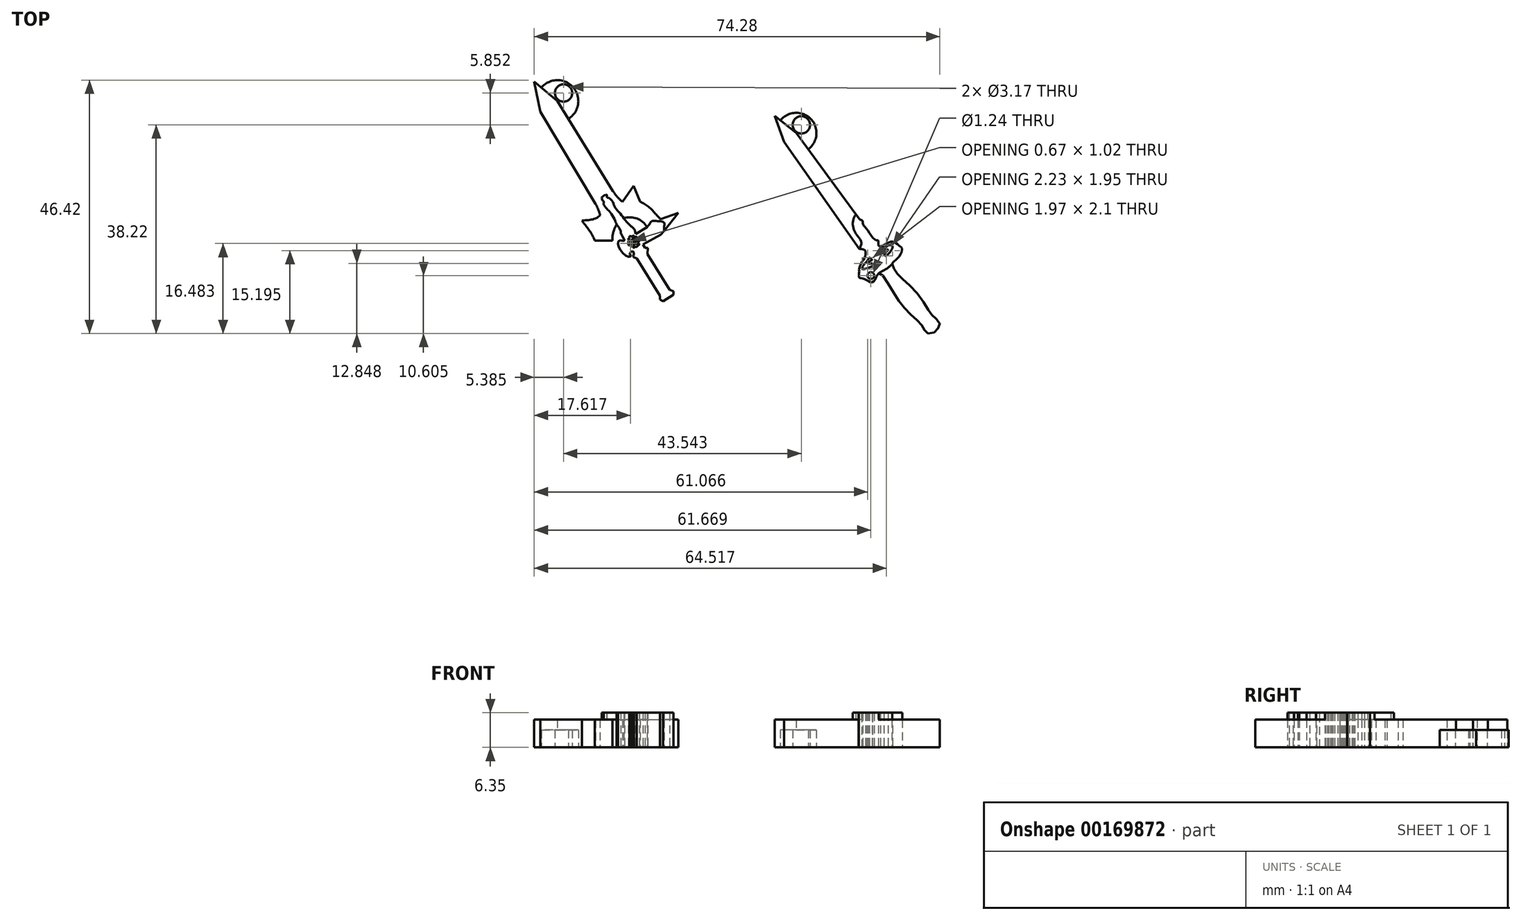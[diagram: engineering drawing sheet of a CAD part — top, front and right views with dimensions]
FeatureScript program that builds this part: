
annotation { "Feature Type Name" : "Feature", "Feature Type Description" : "" }
export const myFeature = defineFeature(function(context is Context, id is Id, definition is map)
    precondition{}
    {
        {
            var Q0;
            Q0=qCreatedBy(makeId("Top.planeOp"),FACE);
            var sketch = newSketch(context, id + "F0", { "sketchPlane" : qUnion([Q0])});
            skLineSegment(sketch, "E0", {"start": v(-47.89, 9.47) * mm, "end": v(-46.77, 3.95) * mm});
            skLineSegment(sketch, "E1", {"start": v(-47.89, 9.47) * mm, "end": v(-43.64, 5.88) * mm});
            skLineSegment(sketch, "E2", {"start": v(-46.77, 3.95) * mm, "end": v(-36.67, -12.95) * mm});
            skLineSegment(sketch, "E3", {"start": v(-43.64, 5.88) * mm, "end": v(-33.47, -10.58) * mm});
            skFitSpline(sketch, "E4", {"points": [v(-36.67, -12.95) * mm, v(-36.26, -13.75) * mm, v(-35.92, -14.65) * mm, v(-35.87, -15.06) * mm, v(-36.67, -15.62) * mm, v(-37.77, -15.9) * mm, v(-39.13, -15.98) * mm], "startDerivative": vector(2.9, -5.08) * mm, "endDerivative": vector(-7.18, 0.14) * mm});
            skFitSpline(sketch, "E5", {"points": [v(-39.13, -15.98) * mm, v(-38.65, -16.7) * mm, v(-37.46, -18.3) * mm, v(-36.8, -19.7) * mm], "startDerivative": vector(1.55, -2.5) * mm, "endDerivative": vector(1.54, -3.95) * mm});
            skLineSegment(sketch, "E6", {"start": v(-36.8, -19.7) * mm, "end": v(-33.56, -19.7) * mm});
            skFitSpline(sketch, "E7", {"points": [v(-33.56, -19.7) * mm, v(-33.56, -19.03) * mm, v(-33.26, -17.7) * mm, v(-32.82, -16.73) * mm], "startDerivative": vector(-0.15, 2.21) * mm, "endDerivative": vector(1.34, 2.63) * mm});
            skFitSpline(sketch, "E8", {"points": [v(-32.82, -16.73) * mm, v(-32, -18) * mm, v(-32.05, -18.37) * mm, v(-31.33, -19.7) * mm, v(-31.77, -19.7) * mm, v(-32.36, -19.7) * mm, v(-32.51, -20.21) * mm, v(-32.2, -21.22) * mm, v(-31.3, -22.27) * mm, v(-30.43, -22.65) * mm, v(-30.2, -22.5) * mm, v(-30.4, -22.17) * mm, v(-30.15, -21.78) * mm, v(-29.87, -21.6) * mm, v(-29.64, -21.88) * mm, v(-29.69, -22.4) * mm, v(-29.8, -22.63) * mm, v(-29.1, -22.93) * mm], "startDerivative": vector(13.43, -16.85) * mm, "endDerivative": vector(15.22, -4.58) * mm});
            skLineSegment(sketch, "E9", {"start": v(-29.1, -22.93) * mm, "end": v(-24.87, -29.77) * mm});
            skLineSegment(sketch, "E10", {"start": v(-23.1, -28.68) * mm, "end": v(-27.13, -22.17) * mm});
            skLineSegment(sketch, "E11", {"start": v(-24.87, -29.77) * mm, "end": v(-24.87, -30.5) * mm});
            skLineSegment(sketch, "E12", {"start": v(-24.87, -30.5) * mm, "end": v(-24.3, -30.8) * mm});
            skLineSegment(sketch, "E13", {"start": v(-24.3, -30.8) * mm, "end": v(-22.35, -29.6) * mm});
            skLineSegment(sketch, "E14", {"start": v(-22.35, -29.6) * mm, "end": v(-22.35, -28.93) * mm});
            skLineSegment(sketch, "E15", {"start": v(-22.35, -28.93) * mm, "end": v(-23.1, -28.68) * mm});
            skFitSpline(sketch, "E16", {"points": [v(-33.47, -10.58) * mm, v(-32.53, -11.84) * mm, v(-31.7, -12.56) * mm], "startDerivative": vector(1.7, -2.5) * mm, "endDerivative": vector(1.85, -1.41) * mm});
            skLineSegment(sketch, "E17", {"start": v(-31.7, -12.56) * mm, "end": v(-29.65, -9.67) * mm});
            skLineSegment(sketch, "E18", {"start": v(-29.65, -9.67) * mm, "end": v(-28.47, -12.56) * mm});
            skFitSpline(sketch, "E19", {"points": [v(-28.47, -12.56) * mm, v(-26.96, -13.47) * mm, v(-25.44, -15.02) * mm, v(-24.72, -15.78) * mm], "startDerivative": vector(4.38, -2.16) * mm, "endDerivative": vector(2.44, -2.49) * mm});
            skLineSegment(sketch, "E20", {"start": v(-24.72, -15.78) * mm, "end": v(-21.5, -14.6) * mm});
            skLineSegment(sketch, "E21", {"start": v(-21.5, -14.6) * mm, "end": v(-24.08, -17.94) * mm});
            skLineSegment(sketch, "E22", {"start": v(-24.08, -17.94) * mm, "end": v(-24.72, -18.63) * mm});
            skLineSegment(sketch, "E23", {"start": v(-24.72, -18.63) * mm, "end": v(-27.94, -20.4) * mm});
            skLineSegment(sketch, "E24", {"start": v(-27.94, -20.4) * mm, "end": v(-27.61, -21) * mm});
            skLineSegment(sketch, "E25", {"start": v(-27.61, -21) * mm, "end": v(-27.09, -21) * mm});
            skLineSegment(sketch, "E26", {"start": v(-27.09, -21) * mm, "end": v(-27.13, -22.17) * mm});
            skArc(sketch, "E27", {"start": v(-27.22, -17.2) * mm, "mid": v(-29.07, -15.64) * mm, "end": v(-31.48, -15.61) * mm});
            skFitSpline(sketch, "E28", {"points": [v(-31.48, -15.61) * mm, v(-30.14, -17.07) * mm, v(-29.6, -17.52) * mm, v(-29.37, -18.14) * mm, v(-29.28, -18.48) * mm], "startDerivative": vector(3.75, -4.48) * mm, "endDerivative": vector(0.5, -1.86) * mm});
            skFitSpline(sketch, "E29", {"points": [v(-29.28, -18.48) * mm, v(-27.22, -17.2) * mm], "startDerivative": vector(2.06, 1.28) * mm, "endDerivative": vector(2.06, 1.28) * mm});
            skFitSpline(sketch, "E30", {"points": [v(-35.52, -11.9) * mm, v(-35.18, -11.48) * mm, v(-34.54, -11.32) * mm, v(-34.58, -11.68) * mm, v(-34.14, -11.93) * mm, v(-33.38, -12.83) * mm, v(-33.14, -13.59) * mm, v(-32.29, -14.55) * mm, v(-31.48, -15.61) * mm], "startDerivative": vector(1.05, 4.71) * mm, "endDerivative": vector(4.53, -6.67) * mm});
            skFitSpline(sketch, "E31", {"points": [v(-35.52, -11.9) * mm, v(-35.38, -12.3) * mm, v(-35.16, -12.49) * mm, v(-35.16, -13) * mm, v(-34.56, -13.9) * mm, v(-34.03, -14.4) * mm, v(-33.12, -15.9) * mm, v(-32.82, -16.73) * mm], "startDerivative": vector(0.68, -4.36) * mm, "endDerivative": vector(1.38, -4.7) * mm});
            skFitSpline(sketch, "E32", {"points": [v(-27.22, -17.2) * mm, v(-26.75, -16.63) * mm, v(-26.37, -16.13) * mm, v(-25.7, -16.1) * mm, v(-24.54, -16.17) * mm, v(-24.08, -16.48) * mm, v(-24.1, -17.4) * mm, v(-24.08, -17.94) * mm], "startDerivative": vector(3.54, 3.78) * mm, "endDerivative": vector(0.59, -3.93) * mm});
            skFitSpline(sketch, "E33", {"points": [v(-30.42, -18.89) * mm, v(-30.42, -19.17) * mm, v(-30.65, -19.36) * mm, v(-30.56, -19.55) * mm, v(-30.32, -19.47) * mm, v(-29.97, -19.65) * mm, v(-29.84, -19.58) * mm, v(-29.8, -19.14) * mm, v(-29.61, -19) * mm, v(-29.64, -18.8) * mm, v(-29.87, -18.86) * mm, v(-30.03, -18.9) * mm, v(-30.42, -18.89) * mm]});
            skFitSpline(sketch, "E34", {"points": [v(-30.57, -19.7) * mm, v(-30.32, -19.86) * mm, v(-30.02, -19.9) * mm, v(-29.97, -20.22) * mm, v(-29.92, -20.61) * mm, v(-30.05, -20.74) * mm, v(-30.32, -20.46) * mm, v(-30.58, -20.5) * mm, v(-30.6, -20.23) * mm, v(-30.57, -19.7) * mm]});
            skFitSpline(sketch, "E35", {"points": [v(-29.39, -19.06) * mm, v(-29.33, -19.31) * mm, v(-29.47, -19.55) * mm, v(-29.46, -19.8) * mm, v(-29.13, -19.77) * mm, v(-28.84, -19.92) * mm, v(-28.7, -19.83) * mm, v(-28.72, -19.46) * mm, v(-28.96, -19.2) * mm, v(-29.3, -19) * mm, v(-29.39, -19.06) * mm]});
            skFitSpline(sketch, "E36", {"points": [v(-29.61, -20.15) * mm, v(-29.57, -20.54) * mm, v(-29.78, -20.84) * mm, v(-29.7, -20.95) * mm, v(-29.6, -20.93) * mm, v(-29.25, -20.83) * mm, v(-29, -20.78) * mm, v(-28.93, -20.58) * mm, v(-28.65, -20.41) * mm, v(-28.68, -20.3) * mm, v(-29.18, -20.3) * mm, v(-29.4, -20.04) * mm, v(-29.61, -20.15) * mm]});
            skLineSegment(sketch, "E37.bottom", {"start": v(-29.85, -19.7) * mm, "end": v(-29.63, -19.7) * mm});
            skLineSegment(sketch, "E37.top", {"start": v(-29.85, -19.97) * mm, "end": v(-29.63, -19.97) * mm});
            skLineSegment(sketch, "E37.left", {"start": v(-29.85, -19.7) * mm, "end": v(-29.85, -19.97) * mm});
            skLineSegment(sketch, "E37.right", {"start": v(-29.63, -19.7) * mm, "end": v(-29.63, -19.97) * mm});
            skLineSegment(sketch, "E38", {"start": v(-2.15, -1.62) * mm, "end": v(11.63, -21.22) * mm});
            skLineSegment(sketch, "E39", {"start": v(0.1, 0.03) * mm, "end": v(11.63, -15.68) * mm});
            skFitSpline(sketch, "E40", {"points": [v(11.63, -21.22) * mm, v(12.7, -21.48) * mm, v(12.73, -22.53) * mm, v(12.21, -23.47) * mm, v(11.63, -24.82) * mm, v(11.63, -25.48) * mm, v(11.63, -26.45) * mm, v(12.64, -26.72) * mm, v(13.69, -27.29) * mm, v(14.47, -26.93) * mm, v(15.22, -25.63) * mm, v(16.13, -26.33) * mm, v(18.33, -29.88) * mm, v(20.37, -32.5) * mm, v(22.57, -34.57) * mm, v(23.44, -35.75) * mm, v(23.98, -36.6) * mm, v(25.46, -36.47) * mm, v(26.21, -35.57) * mm, v(26.33, -34.66) * mm, v(25.16, -33.55) * mm, v(24.23, -32.29) * mm, v(21.85, -28.89) * mm, v(19.14, -26.33) * mm, v(18.14, -25) * mm, v(17.66, -23.95) * mm, v(18.63, -22.98) * mm, v(19.5, -21.22) * mm, v(19.02, -20.67) * mm, v(18, -19.94) * mm, v(16.82, -20.13) * mm, v(15.38, -20.73) * mm, v(15.13, -20.3) * mm, v(15.1, -19.67) * mm, v(14.6, -19.55) * mm, v(12.97, -17.5) * mm, v(12.3, -16.63) * mm, v(12.24, -16.1) * mm, v(11.88, -15.88) * mm, v(11.63, -15.68) * mm], "startDerivative": vector(56.2, -1.17) * mm, "endDerivative": vector(-16.89, 17.47) * mm});
            skLineSegment(sketch, "E41", {"start": v(-3.86, 3.14) * mm, "end": v(-2.15, -1.62) * mm});
            skLineSegment(sketch, "E42", {"start": v(0.1, 0.03) * mm, "end": v(-3.86, 3.14) * mm});
            skPoint(sketch, "E43.start.orphan", {"position": v(-8.49, 9.47) * mm});
            skFitSpline(sketch, "E44", {"points": [v(14, -23.23) * mm, v(13.35, -23.8) * mm, v(13.68, -23.93) * mm, v(14.8, -23.36) * mm, v(16.7, -21.67) * mm, v(16.9, -21.33) * mm, v(16.2, -21.49) * mm, v(15.98, -21.57) * mm, v(15.38, -20.73) * mm], "startDerivative": vector(-7.7, -5.02) * mm, "endDerivative": vector(-5.02, 8.35) * mm});
            skFitSpline(sketch, "E45", {"points": [v(14, -23.23) * mm, v(13.52, -22.8) * mm, v(12.93, -22.67) * mm, v(12.73, -22.53) * mm], "startDerivative": vector(-1.1, 1.33) * mm, "endDerivative": vector(-0.68, 0.64) * mm});
            skFitSpline(sketch, "E46", {"points": [v(15.22, -25.63) * mm, v(17.13, -24.5) * mm, v(17.66, -23.95) * mm], "startDerivative": vector(3.52, 1.9) * mm, "endDerivative": vector(1.15, 1.43) * mm});
            skCircle(sketch, "E47", {"center": v(13.78, -26.1) * mm, "radius": 0.62 * mm});
            skArc(sketch, "E48", {"start": v(-41.62, 2.62) * mm, "mid": v(-40.74, 8.39) * mm, "end": v(-46.57, 8.36) * mm});
            skCircle(sketch, "E49", {"center": v(-42.5, 7.37) * mm, "radius": 1.59 * mm});
            skArc(sketch, "E50", {"start": v(2.3, -2.95) * mm, "mid": v(2.77, 2.6) * mm, "end": v(-2.8, 2.32) * mm});
            skCircle(sketch, "E51", {"center": v(1.04, 1.52) * mm, "radius": 1.59 * mm});
            skFitSpline(sketch, "E52", {"points": [v(11.03, -14.86) * mm, v(10.62, -15.63) * mm, v(10.48, -16.83) * mm, v(10.75, -17.92) * mm, v(11.47, -19) * mm, v(12.03, -20.1) * mm, v(11.63, -21.22) * mm], "startDerivative": vector(-3.14, -4.88) * mm, "endDerivative": vector(-3.7, -6.63) * mm});
            skFitSpline(sketch, "E53", {"points": [v(15.51, -20.96) * mm, v(17.07, -20.52) * mm, v(17.68, -20.6) * mm, v(17.58, -21.33) * mm, v(16.48, -22.48) * mm, v(16.2, -22.18) * mm], "startDerivative": vector(6.32, 2.09) * mm, "endDerivative": vector(-1.57, 3.48) * mm});
            skFitSpline(sketch, "E54", {"points": [v(13, -23.53) * mm, v(12.3, -24.41) * mm, v(12.22, -24.9) * mm, v(12.92, -24.78) * mm, v(14.13, -24.31) * mm, v(14.04, -23.84) * mm], "startDerivative": vector(-3.42, -3.59) * mm, "endDerivative": vector(-1.61, 3.27) * mm});
            skFitSpline(sketch, "E55", {"points": [v(13, -23.53) * mm, v(13.52, -22.8) * mm], "startDerivative": vector(0.52, 0.73) * mm, "endDerivative": vector(0.52, 0.73) * mm});
            skSolve(sketch);
        }
        {
            var Q0;
            Q0=makeQuery(id+"F0.imprint","IMPRINT",FACE,{"disambiguationData":[TD([[makeQuery(id+"F0.imprint","IMPRINT",EDGE,{"derivedFrom":sQuery(id+"F0.wireOp",EDGE,"E8")}),1.0]])]});
            var Q1;
            {var subQ0=sQuery(id+"F0.wireOp",EDGE,"E44");Q1=makeQuery(id+"F0.imprint","IMPRINT",FACE,{"disambiguationData":[TD([[makeQuery(id+"F0.imprint","IMPRINT",EDGE,{"derivedFrom":subQ0}),1.0]])]});}
            var Q2;
            {var subQ6=sQuery(id+"F0.wireOp",EDGE,"E46");Q2=makeQuery(id+"F0.imprint","IMPRINT",FACE,{"disambiguationData":[TD([[makeQuery(id+"F0.imprint","IMPRINT",EDGE,{"derivedFrom":subQ6}),1.0]])]});}
            extrude(context, id + "F1", {"entities" : qUnion([Q0, Q1, Q2]), "depth" : 6.35 * mm});
        }
        {
            var Q0;
            Q0=makeQuery(id+"F0.imprint","IMPRINT",FACE,{"disambiguationData":[TD([[makeQuery(id+"F0.imprint","IMPRINT",EDGE,{"derivedFrom":sQuery(id+"F0.wireOp",EDGE,"E0")}),1.0]])]});
            var Q1;
            {var subQ3=sQuery(id+"F0.wireOp",EDGE,"E38");Q1=makeQuery(id+"F0.imprint","IMPRINT",FACE,{"disambiguationData":[TD([[makeQuery(id+"F0.imprint","IMPRINT",EDGE,{"derivedFrom":subQ3}),1.0]])]});}
            var Q2;
            {var subQ0=sQuery(id+"F0.wireOp",EDGE,"E46");Q2=makeQuery(id+"F0.imprint","IMPRINT",FACE,{"disambiguationData":[TD([[makeQuery(id+"F0.imprint","IMPRINT",EDGE,{"derivedFrom":subQ0}),-1.0]])]});}
            extrude(context, id + "F2", {"entities" : qUnion([Q0, Q1, Q2]), "operationType" : NewBodyOperationType.ADD, "depth" : 5.08 * mm});
        }
        {
            var Q0;
            {var subQ3=sQuery(id+"F0.wireOp",EDGE,"E48");Q0=makeQuery(id+"F0.imprint","IMPRINT",FACE,{"disambiguationData":[TD([[makeQuery(id+"F0.imprint","IMPRINT",EDGE,{"derivedFrom":subQ3}),1.0]])]});}
            var Q1;
            {var subQ3=sQuery(id+"F0.wireOp",EDGE,"E50");Q1=makeQuery(id+"F0.imprint","IMPRINT",FACE,{"disambiguationData":[TD([[makeQuery(id+"F0.imprint","IMPRINT",EDGE,{"derivedFrom":subQ3}),1.0]])]});}
            extrude(context, id + "F3", {"entities" : qUnion([Q0, Q1]), "operationType" : NewBodyOperationType.ADD, "depth" : 3.17 * mm});
        }
    });
